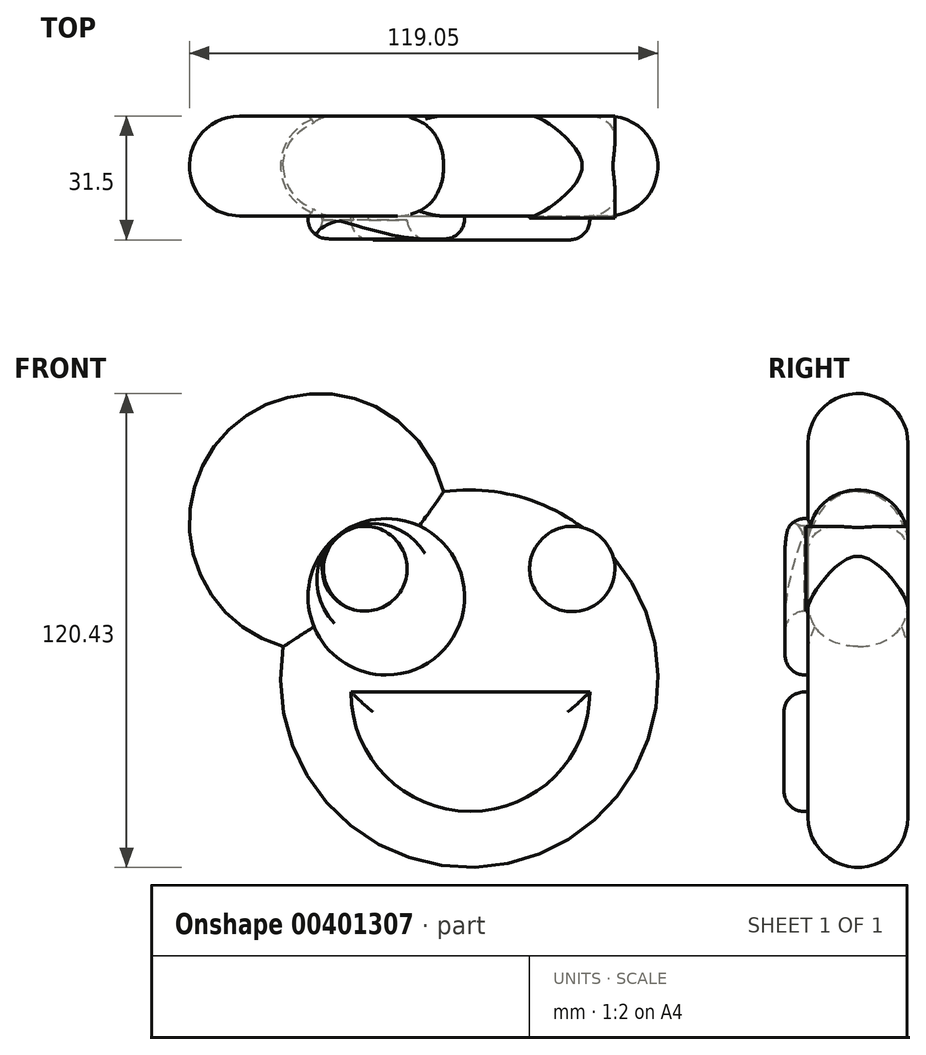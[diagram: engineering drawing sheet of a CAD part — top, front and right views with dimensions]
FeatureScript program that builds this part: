
annotation { "Feature Type Name" : "Feature", "Feature Type Description" : "" }
export const myFeature = defineFeature(function(context is Context, id is Id, definition is map)
    precondition{}
    {
        {
            var Q0;
            Q0=qCreatedBy(makeId("Front.planeOp"),FACE);
            var sketch = newSketch(context, id + "F0", { "sketchPlane" : qUnion([Q0])});
            skCircle(sketch, "E0", {"center": v(0, 0) * mm, "radius": 47.97 * mm});
            skArc(sketch, "E1", {"start": v(-6.49, 47.53) * mm, "mid": v(-61.07, 63.26) * mm, "end": v(-47.27, 8.16) * mm});
            skArc(sketch, "E2.MirrorCS", {"start": v(6.49, 47.53) * mm, "mid": v(61.07, 63.26) * mm, "end": v(47.27, 8.16) * mm});
            skSolve(sketch);
        }
        {
            var Q0;
            {var subQ0=sQuery(id+"F0.wireOp",EDGE,"qMnfbMMB-3m1s-uUW1-9r4w-OCcZsqSqAnbS");var subQ1=sQuery(id+"F0.wireOp",EDGE,"E0");var subQ2=makeQuery(id+"F0.imprint","INTERSECT",VERTEX,{"disambiguationData":[OD(0.0)],"derivedFrom":[subQ1,subQ0]});Q0=makeQuery(id+"F0.imprint","IMPRINT",FACE,{"disambiguationData":[TD([[makeQuery(id+"F0.imprint","IMPRINT",EDGE,{"disambiguationData":[TD([[subQ2,1.0]])],"derivedFrom":subQ1}),-1.0]])]});}
            var Q1;
            {var subQ0=sQuery(id+"F0.wireOp",EDGE,"qMnfbMMB-3m1s-uUW1-9r4w-OCcZsqSqAnbS");var subQ1=sQuery(id+"F0.wireOp",EDGE,"E0");var subQ2=makeQuery(id+"F0.imprint","INTERSECT",VERTEX,{"disambiguationData":[OD(0.0)],"derivedFrom":[subQ1,subQ0]});Q1=makeQuery(id+"F0.imprint","IMPRINT",FACE,{"disambiguationData":[TD([[makeQuery(id+"F0.imprint","IMPRINT",EDGE,{"disambiguationData":[TD([[subQ2,1.0]])],"derivedFrom":subQ1}),1.0]])]});}
            var Q2;
            {var subQ0=sQuery(id+"F0.wireOp",EDGE,"E1");var subQ1=sQuery(id+"F0.wireOp",EDGE,"E0");var subQ2=makeQuery(id+"F0.imprint","INTERSECT",VERTEX,{"disambiguationData":[OD(0.0)],"derivedFrom":[subQ1,subQ0]});Q2=makeQuery(id+"F0.imprint","IMPRINT",FACE,{"disambiguationData":[TD([[makeQuery(id+"F0.imprint","IMPRINT",EDGE,{"disambiguationData":[TD([[subQ2,-1.0]])],"derivedFrom":subQ1}),1.0]])]});}
            var Q3;
            {var subQ0=sQuery(id+"F0.wireOp",EDGE,"E1");var subQ1=sQuery(id+"F0.wireOp",EDGE,"E0");var subQ2=makeQuery(id+"F0.imprint","INTERSECT",VERTEX,{"disambiguationData":[OD(0.0)],"derivedFrom":[subQ1,subQ0]});Q3=makeQuery(id+"F0.imprint","IMPRINT",FACE,{"disambiguationData":[TD([[makeQuery(id+"F0.imprint","IMPRINT",EDGE,{"disambiguationData":[TD([[subQ2,-1.0]])],"derivedFrom":subQ1}),-1.0]])]});}
            var Q4;
            {var subQ0=sQuery(id+"F0.wireOp",EDGE,"E2.MirrorCS");Q4=makeQuery(id+"F0.imprint","IMPRINT",FACE,{"disambiguationData":[TD([[makeQuery(id+"F0.imprint","IMPRINT",EDGE,{"derivedFrom":subQ0}),-1.0]])]});}
            extrude(context, id + "F1", {"entities" : qUnion([Q0, Q1, Q2, Q3, Q4]), "depth" : 25.4 * mm});
        }
        {
            var Q0;
            Q0=makeQuery(id+"F1.opExtrude","CAP_FACE",FACE,{"disambiguationData":[OSD([sQuery(id+"F0.wireOp",EDGE,"E0"),sQuery(id+"F0.wireOp",EDGE,"E1"),sQuery(id+"F0.wireOp",EDGE,"E2.MirrorCS")])],"isStart":false});
            fillet(context, id + "F2", {"entities" : qUnion([Q0]), "radius" : 12.7 * mm, "tangentPropagation" : true, "allowEdgeOverflow" : false});
        }
        {
            var Q0;
            Q0=makeQuery(id+"F1.opExtrude","CAP_FACE",FACE,{"disambiguationData":[OSD([sQuery(id+"F0.wireOp",EDGE,"E0"),sQuery(id+"F0.wireOp",EDGE,"E1"),sQuery(id+"F0.wireOp",EDGE,"E2.MirrorCS")])],"isStart":true});
            fillet(context, id + "F3", {"entities" : qUnion([Q0]), "radius" : 12.7 * mm, "tangentPropagation" : true, "allowEdgeOverflow" : false});
        }
        {
            var Q0;
            Q0=qCreatedBy(makeId("Front.planeOp"),FACE);
            var sketch = newSketch(context, id + "F4", { "sketchPlane" : qUnion([Q0])});
            skCircle(sketch, "E3", {"center": v(-21.08, 20.8) * mm, "radius": 19.87 * mm});
            skCircle(sketch, "E4.MirrorC", {"center": v(21.08, 20.8) * mm, "radius": 19.87 * mm});
            skCircle(sketch, "E5", {"center": v(-26.58, 27.95) * mm, "radius": 10.8 * mm});
            skCircle(sketch, "E6.MirrorC", {"center": v(26.58, 27.95) * mm, "radius": 10.8 * mm});
            skSolve(sketch);
        }
        {
            var Q0;
            Q0=makeQuery(id+"F4.imprint","IMPRINT",FACE,{"disambiguationData":[TD([[makeQuery(id+"F4.imprint","IMPRINT",EDGE,{"derivedFrom":sQuery(id+"F4.wireOp",EDGE,"E4.MirrorC")}),-1.0]])]});
            var Q1;
            Q1=makeQuery(id+"F4.imprint","IMPRINT",FACE,{"disambiguationData":[TD([[makeQuery(id+"F4.imprint","IMPRINT",EDGE,{"derivedFrom":sQuery(id+"F4.wireOp",EDGE,"E3")}),1.0]])]});
            extrude(context, id + "F5", {"entities" : qUnion([Q0, Q1]), "operationType" : NewBodyOperationType.ADD, "depth" : 31.24 * mm});
        }
        {
            var Q0;
            Q0=makeQuery(id+"F5.opExtrude","CAP_FACE",FACE,{"disambiguationData":[OSD([sQuery(id+"F4.wireOp",EDGE,"E4.MirrorC"),sQuery(id+"F4.wireOp",EDGE,"E6.MirrorC")])],"isStart":false});
            var Q1;
            Q1=makeQuery(id+"F5.opExtrude","CAP_FACE",FACE,{"disambiguationData":[OSD([sQuery(id+"F4.wireOp",EDGE,"E3"),sQuery(id+"F4.wireOp",EDGE,"E5")])],"isStart":false});
            fillet(context, id + "F6", {"entities" : qUnion([Q0, Q1]), "radius" : 5.08 * mm, "tangentPropagation" : true, "allowEdgeOverflow" : false});
        }
        {
            var Q0;
            Q0=qCreatedBy(makeId("Front.planeOp"),FACE);
            var sketch = newSketch(context, id + "F7", { "sketchPlane" : qUnion([Q0])});
            skCircle(sketch, "E7", {"center": v(-26.18, 27.88) * mm, "radius": 10.84 * mm});
            skPoint(sketch, "E7.first.point", {"position": v(-33.54, 35.83) * mm});
            skPoint(sketch, "E7.second.point", {"position": v(-19.06, 19.7) * mm});
            skPoint(sketch, "E7.third.point", {"position": v(-15.58, 30.15) * mm});
            skCircle(sketch, "E8.MirrorC", {"center": v(26.18, 27.88) * mm, "radius": 10.84 * mm});
            skSolve(sketch);
        }
        {
            var Q0;
            Q0=makeQuery(id+"F7.imprint","IMPRINT",FACE,{"disambiguationData":[TD([[makeQuery(id+"F7.imprint","IMPRINT",EDGE,{"derivedFrom":sQuery(id+"F7.wireOp",EDGE,"E7")}),1.0]])]});
            extrude(context, id + "F8", {"entities" : qUnion([Q0]), "operationType" : NewBodyOperationType.ADD, "depth" : 26.42 * mm});
        }
        {
            var Q0;
            Q0=qSketchRegion(id+"F7",true);
            extrude(context, id + "F9", {"entities" : qUnion([Q0]), "operationType" : NewBodyOperationType.ADD, "depth" : 25.9 * mm});
        }
        {
            var Q0;
            {var subQ0=sQuery(id+"F0.wireOp",EDGE,"E1");var subQ1=sQuery(id+"F0.wireOp",EDGE,"E0");var subQ2=sQuery(id+"F0.wireOp",EDGE,"E2.MirrorCS");Q0=makeQuery(id+"F5.boolean.opBoolean","SPLIT",FACE,{"disambiguationData":[TD([makeQuery(id+"F2.opFillet","BLEND_FACE",FACE,{"disambiguationData":[OSD([subQ1]),TDD([makeQuery(id+"F1.opExtrude","CAP_EDGE",EDGE,{"disambiguationData":[OSD([subQ1]),TDD([makeQuery(id+"F0.imprint","IMPRINT",EDGE,{"disambiguationData":[TD([[makeQuery(id+"F0.imprint","INTERSECT",VERTEX,{"disambiguationData":[OD(0.0)],"derivedFrom":[subQ1,subQ0]}),1.0]])],"derivedFrom":subQ1})])],"isStart":false})])]}),makeQuery(id+"F2.opFillet","BLEND_FACE",FACE,{"disambiguationData":[OSD([subQ1]),TDD([makeQuery(id+"F1.opExtrude","CAP_EDGE",EDGE,{"disambiguationData":[OSD([subQ1]),TDD([makeQuery(id+"F0.imprint","IMPRINT",EDGE,{"disambiguationData":[TD([[makeQuery(id+"F0.imprint","INTERSECT",VERTEX,{"disambiguationData":[OD(1.0)],"derivedFrom":[subQ1,subQ0]}),-1.0]])],"derivedFrom":subQ1})])],"isStart":false})])]}),makeQuery(id+"F5.opExtrude","SWEPT_FACE",FACE,{"disambiguationData":[OSD([sQuery(id+"F4.wireOp",EDGE,"E3")])]}),makeQuery(id+"F5.opExtrude","SWEPT_FACE",FACE,{"disambiguationData":[OSD([sQuery(id+"F4.wireOp",EDGE,"E4.MirrorC")])]})])],"derivedFrom":makeQuery(id+"F1.opExtrude","CAP_FACE",FACE,{"disambiguationData":[OSD([subQ1,subQ0,subQ2])],"isStart":false})});}
            var sketch = newSketch(context, id + "F10", { "sketchPlane" : qUnion([Q0])});
            skLineSegment(sketch, "E9", {"start": v(-30.06, -3.4) * mm, "end": v(30.61, -3.4) * mm});
            skArc(sketch, "E10", {"start": v(30.61, -3.4) * mm, "mid": v(0.27, -33.73) * mm, "end": v(-30.06, -3.4) * mm});
            skSolve(sketch);
        }
        {
            var Q0;
            Q0=makeQuery(id+"F10.imprint","IMPRINT",FACE,{"disambiguationData":[TD([[makeQuery(id+"F10.imprint","IMPRINT",EDGE,{"derivedFrom":sQuery(id+"F10.wireOp",EDGE,"E9")}),-1.0]])]});
            extrude(context, id + "F11", {"entities" : qUnion([Q0]), "operationType" : NewBodyOperationType.ADD, "depth" : 6.1 * mm});
        }
        {
            var Q0;
            Q0=makeQuery(id+"F11.opExtrude","CAP_FACE",FACE,{"disambiguationData":[OSD([sQuery(id+"F10.wireOp",EDGE,"E9"),sQuery(id+"F10.wireOp",EDGE,"E10")])],"isStart":false});
            fillet(context, id + "F12", {"entities" : qUnion([Q0]), "radius" : 5.08 * mm, "tangentPropagation" : true, "allowEdgeOverflow" : false});
        }
    });
